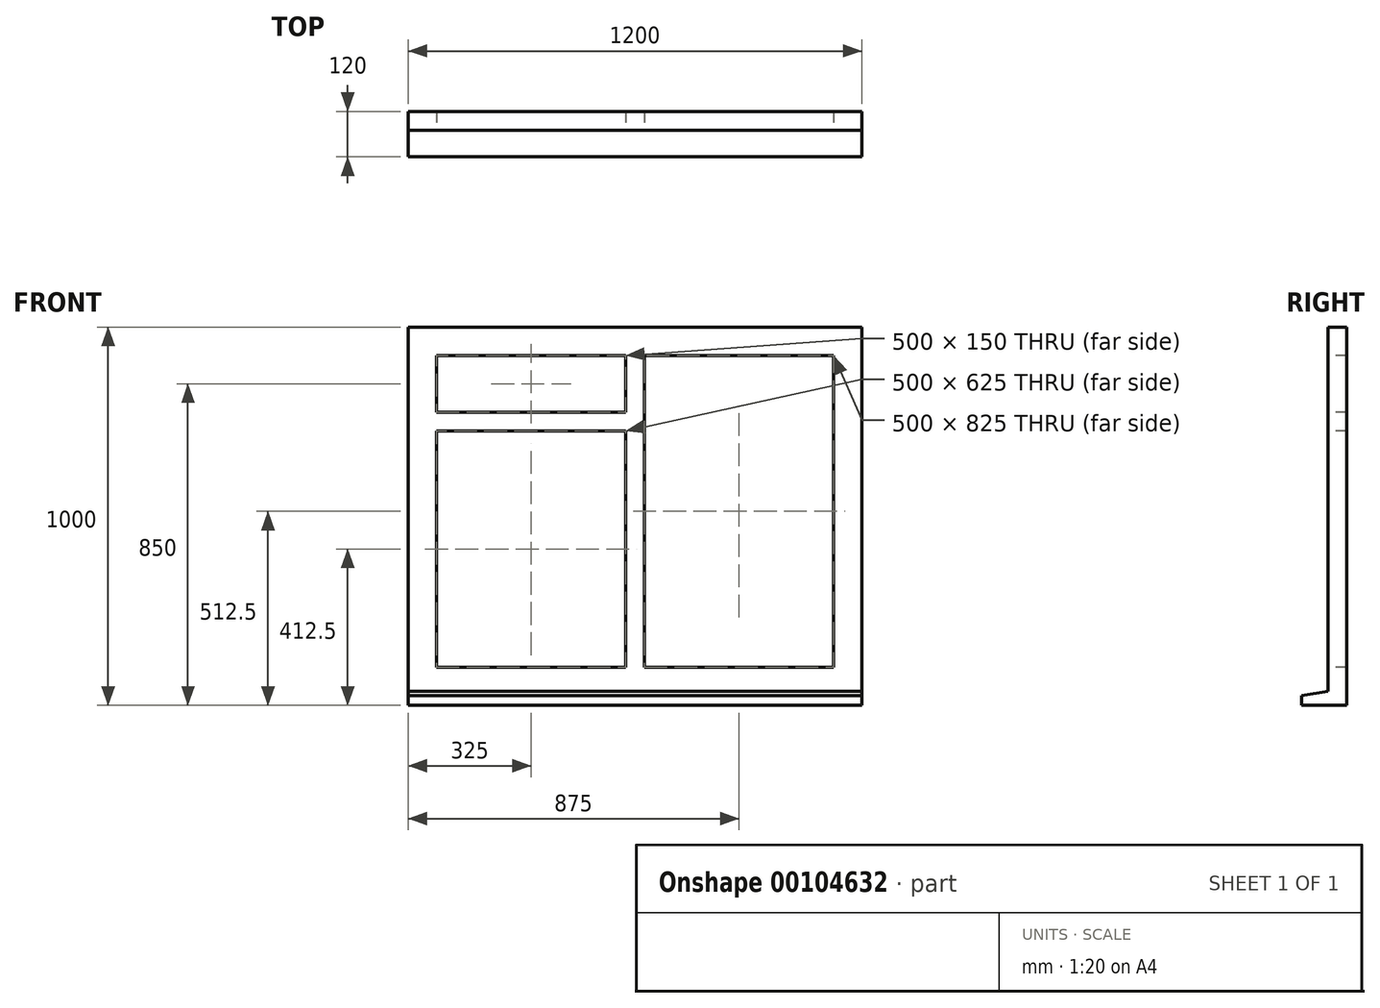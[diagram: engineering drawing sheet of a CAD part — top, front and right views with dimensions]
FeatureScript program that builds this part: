
annotation { "Feature Type Name" : "Feature", "Feature Type Description" : "" }
export const myFeature = defineFeature(function(context is Context, id is Id, definition is map)
    precondition{}
    {
        {
            var Q0;
            Q0=qCreatedBy(makeId("Front.planeOp"),FACE);
            var sketch = newSketch(context, id + "F0", { "sketchPlane" : qUnion([Q0])});
            skLineSegment(sketch, "E0.bottom", {"start": v(0, 0) * mm, "end": v(1200, 0) * mm});
            skLineSegment(sketch, "E0.top", {"start": v(0, -1000) * mm, "end": v(1200, -1000) * mm});
            skLineSegment(sketch, "E0.left", {"start": v(0, 0) * mm, "end": v(0, -1000) * mm});
            skLineSegment(sketch, "E0.right", {"start": v(1200, 0) * mm, "end": v(1200, -1000) * mm});
            skLineSegment(sketch, "E1.bottom", {"start": v(625, -75) * mm, "end": v(1125, -75) * mm});
            skLineSegment(sketch, "E1.top", {"start": v(625, -900) * mm, "end": v(1125, -900) * mm});
            skLineSegment(sketch, "E1.left", {"start": v(625, -75) * mm, "end": v(625, -900) * mm});
            skLineSegment(sketch, "E1.right", {"start": v(1125, -75) * mm, "end": v(1125, -900) * mm});
            skLineSegment(sketch, "E2.bottom", {"start": v(75, -275) * mm, "end": v(575, -275) * mm});
            skLineSegment(sketch, "E2.top", {"start": v(75, -900) * mm, "end": v(575, -900) * mm});
            skLineSegment(sketch, "E2.left", {"start": v(75, -275) * mm, "end": v(75, -900) * mm});
            skLineSegment(sketch, "E2.right", {"start": v(575, -275) * mm, "end": v(575, -900) * mm});
            skLineSegment(sketch, "E3.bottom", {"start": v(75, -75) * mm, "end": v(575, -75) * mm});
            skLineSegment(sketch, "E3.top", {"start": v(75, -225) * mm, "end": v(575, -225) * mm});
            skLineSegment(sketch, "E3.left", {"start": v(75, -75) * mm, "end": v(75, -225) * mm});
            skLineSegment(sketch, "E3.right", {"start": v(575, -75) * mm, "end": v(575, -225) * mm});
            skPoint(sketch, "E4.firstSnap0", {"position": v(325, -225) * mm});
            skSolve(sketch);
        }
        {
            var Q0;
            Q0=qSketchRegion(id+"F0",true);
            extrude(context, id + "F1", {"entities" : qUnion([Q0]), "oppositeDirection" : true, "depth" : 50 * mm});
        }
        {
            var Q0;
            Q0=makeQuery(id+"F1.opExtrude","SWEPT_FACE",FACE,{"disambiguationData":[OSD([sQuery(id+"F0.wireOp",EDGE,"E0.right")])]});
            var sketch = newSketch(context, id + "F2", { "sketchPlane" : qUnion([Q0])});
            skLineSegment(sketch, "E5", {"start": v(0, -1000) * mm, "end": v(-70, -1000) * mm});
            skLineSegment(sketch, "E6", {"start": v(0, -962.66) * mm, "end": v(-70, -975) * mm});
            skLineSegment(sketch, "E7", {"start": v(-70, -975) * mm, "end": v(-70, -1000) * mm});
            skLineSegment(sketch, "E8", {"start": v(0, -1000) * mm, "end": v(0, -962.66) * mm});
            skSolve(sketch);
        }
        {
            var Q0;
            Q0=qSketchRegion(id+"F2",true);
            extrude(context, id + "F3", {"entities" : qUnion([Q0]), "operationType" : NewBodyOperationType.ADD, "oppositeDirection" : true, "depth" : 1200 * mm});
        }
    });
